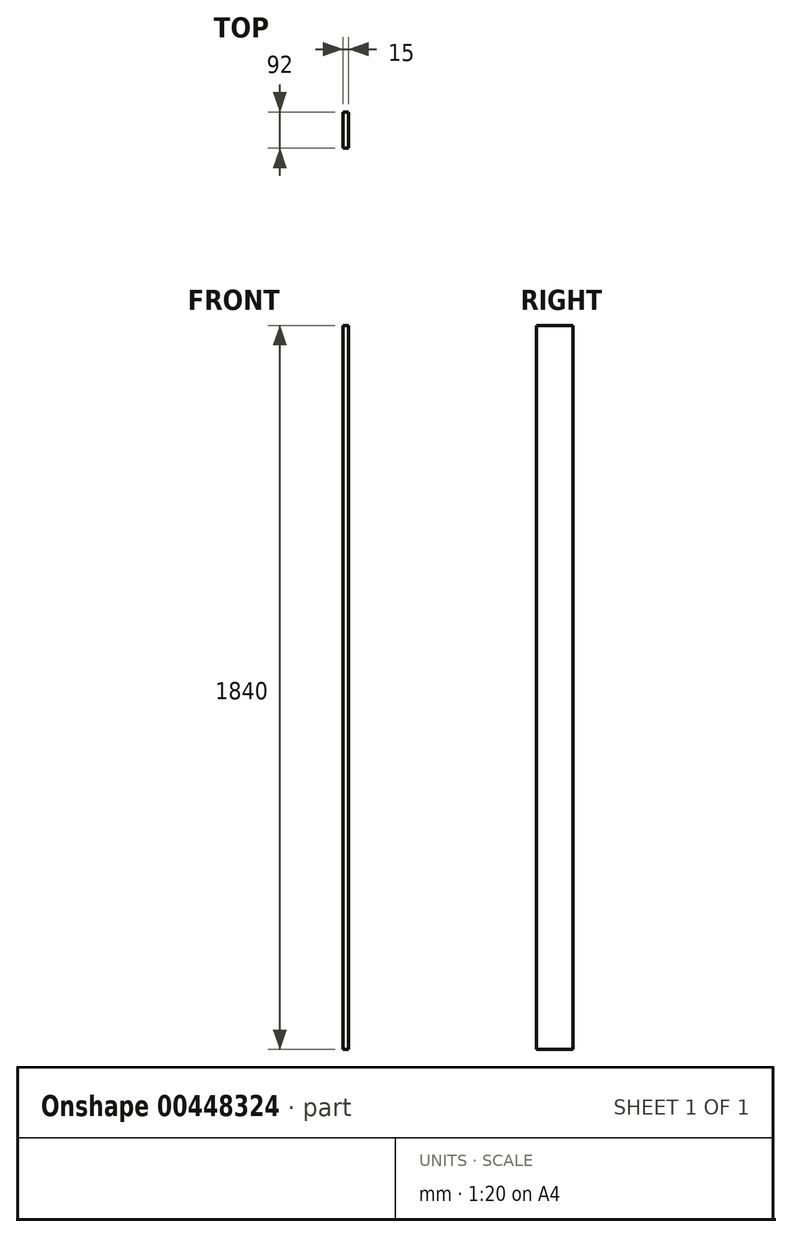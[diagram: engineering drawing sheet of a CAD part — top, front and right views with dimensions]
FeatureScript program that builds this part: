
annotation { "Feature Type Name" : "Feature", "Feature Type Description" : "" }
export const myFeature = defineFeature(function(context is Context, id is Id, definition is map)
    precondition{}
    {
        {
            var Q0;
            Q0=qCreatedBy(makeId("Right.planeOp"),FACE);
            var sketch = newSketch(context, id + "F0", { "sketchPlane" : qUnion([Q0])});
            skLineSegment(sketch, "E0.bottom", {"start": v(0, 0) * mm, "end": v(-92, 0) * mm});
            skLineSegment(sketch, "E0.top", {"start": v(0, 1840) * mm, "end": v(-92, 1840) * mm});
            skLineSegment(sketch, "E0.left", {"start": v(0, 0) * mm, "end": v(0, 1840) * mm});
            skLineSegment(sketch, "E0.right", {"start": v(-92, 0) * mm, "end": v(-92, 1840) * mm});
            skSolve(sketch);
        }
        {
            var Q0;
            Q0=makeQuery(id+"F0.imprint","IMPRINT",FACE,{"disambiguationData":[TD([[makeQuery(id+"F0.imprint","IMPRINT",EDGE,{"derivedFrom":sQuery(id+"F0.wireOp",EDGE,"E0.bottom")}),-1.0]])]});
            extrude(context, id + "F1", {"entities" : qUnion([Q0]), "depth" : 15 * mm});
        }
    });
